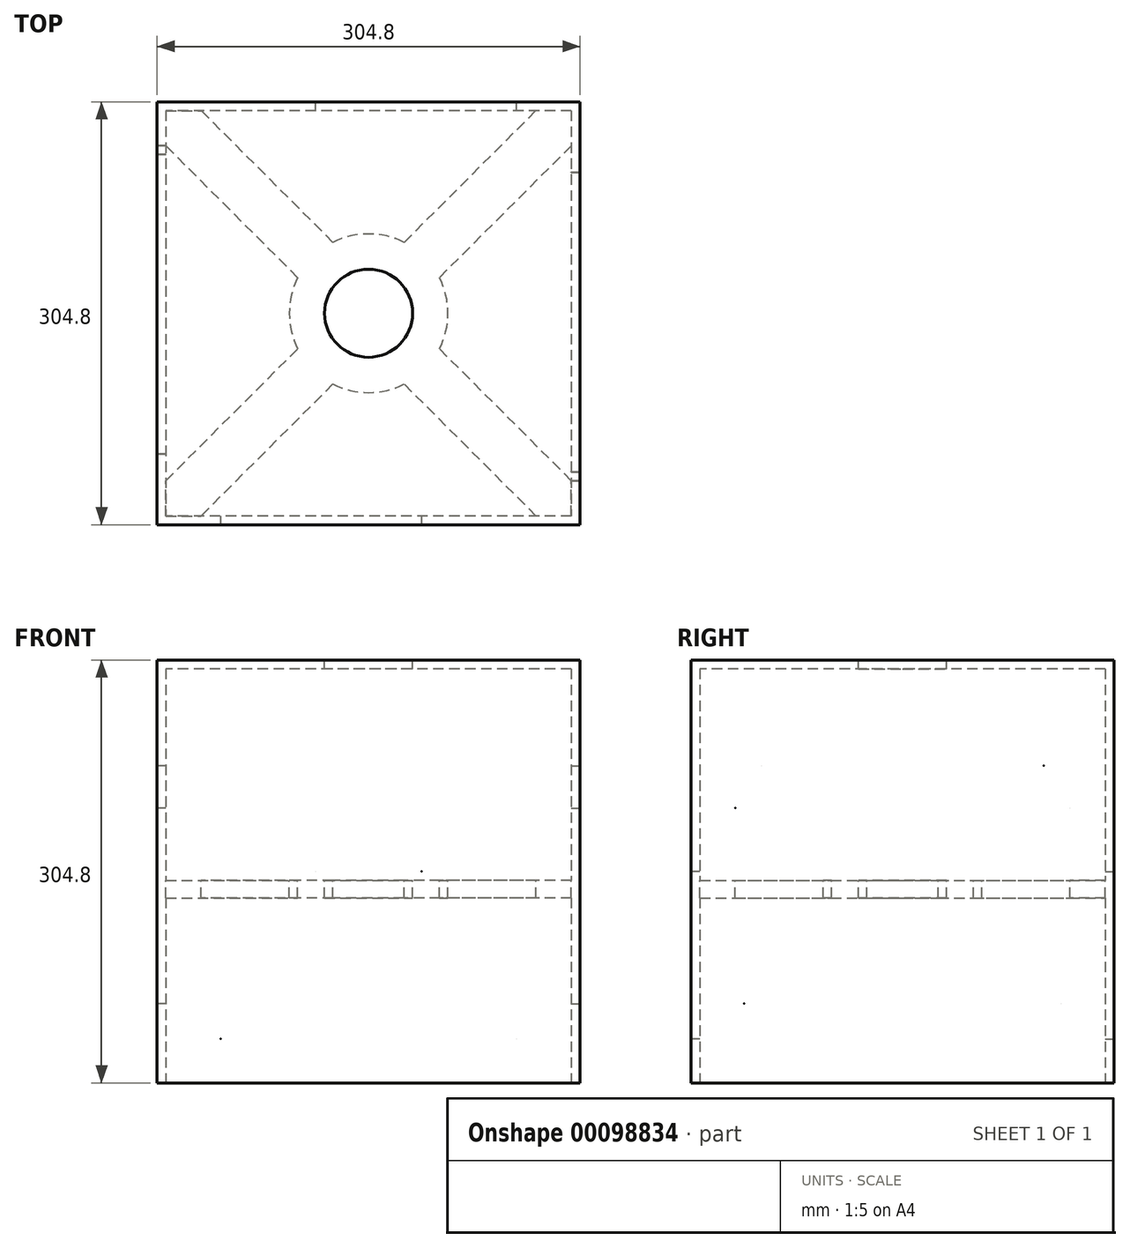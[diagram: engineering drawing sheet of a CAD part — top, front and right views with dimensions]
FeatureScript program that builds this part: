
annotation { "Feature Type Name" : "Feature", "Feature Type Description" : "" }
export const myFeature = defineFeature(function(context is Context, id is Id, definition is map)
    precondition{}
    {
        {
            var Q0;
            Q0=qCreatedBy(makeId("Top.planeOp"),FACE);
            var sketch = newSketch(context, id + "F0", { "sketchPlane" : qUnion([Q0])});
            skLineSegment(sketch, "E0.bottom", {"start": v(152.4, -152.4) * mm, "end": v(-152.4, -152.4) * mm});
            skLineSegment(sketch, "E0.top", {"start": v(152.4, 152.4) * mm, "end": v(-152.4, 152.4) * mm});
            skLineSegment(sketch, "E0.left", {"start": v(152.4, -152.4) * mm, "end": v(152.4, 152.4) * mm});
            skLineSegment(sketch, "E0.right", {"start": v(-152.4, -152.4) * mm, "end": v(-152.4, 152.4) * mm});
            skPoint(sketch, "E0.middle", {"position": v(0, 0) * mm});
            skLineSegment(sketch, "E1.bottom", {"start": v(146.05, 146.05) * mm, "end": v(-146.05, 146.05) * mm});
            skLineSegment(sketch, "E1.top", {"start": v(146.05, -146.05) * mm, "end": v(-146.05, -146.05) * mm});
            skLineSegment(sketch, "E1.left", {"start": v(146.05, 146.05) * mm, "end": v(146.05, -146.05) * mm});
            skLineSegment(sketch, "E1.right", {"start": v(-146.05, 146.05) * mm, "end": v(-146.05, -146.05) * mm});
            skSolve(sketch);
        }
        {
            var Q0;
            Q0 = qSketchRegion(id + "F0", true);
            extrude(context, id + "F1", {"entities" : qUnion([Q0]), "endBound" : BoundingType.SYMMETRIC, "depth" : 304.8 * mm});
        }
        {
            var Q0;
            Q0=makeQuery(id+"F1.opExtrude","CAP_FACE",FACE,{"disambiguationData":[OSD([sQuery(id+"F0.wireOp",EDGE,"E0.bottom"),sQuery(id+"F0.wireOp",EDGE,"E0.top"),sQuery(id+"F0.wireOp",EDGE,"E0.left"),sQuery(id+"F0.wireOp",EDGE,"E0.right"),sQuery(id+"F0.wireOp",EDGE,"E1.bottom"),sQuery(id+"F0.wireOp",EDGE,"E1.top"),sQuery(id+"F0.wireOp",EDGE,"E1.left"),sQuery(id+"F0.wireOp",EDGE,"E1.right")])],"isStart":false});
            var sketch = newSketch(context, id + "F2", { "sketchPlane" : qUnion([Q0])});
            skLineSegment(sketch, "E2.bottom", {"start": v(152.4, -152.4) * mm, "end": v(-152.4, -152.4) * mm});
            skLineSegment(sketch, "E2.top", {"start": v(152.4, 152.4) * mm, "end": v(-152.4, 152.4) * mm});
            skLineSegment(sketch, "E2.left", {"start": v(152.4, -152.4) * mm, "end": v(152.4, 152.4) * mm});
            skLineSegment(sketch, "E2.right", {"start": v(-152.4, -152.4) * mm, "end": v(-152.4, 152.4) * mm});
            skPoint(sketch, "E2.middle", {"position": v(0, 0) * mm});
            skSolve(sketch);
        }
        {
            var Q0;
            Q0 = qSketchRegion(id + "F2", true);
            extrude(context, id + "F3", {"entities" : qUnion([Q0]), "operationType" : NewBodyOperationType.ADD, "oppositeDirection" : true, "depth" : 6.35 * mm});
        }
        {
            var Q0;
            Q0=makeQuery(id+"F1.opExtrude","SWEPT_FACE",FACE,{"disambiguationData":[OSD([sQuery(id+"F0.wireOp",EDGE,"E0.bottom")])]});
            var sketch = newSketch(context, id + "F4", { "sketchPlane" : qUnion([Q0])});
            skLineSegment(sketch, "E3", {"start": v(-152.4, 152.4) * mm, "end": v(152.4, -152.4) * mm});
            skLineSegment(sketch, "E4", {"start": v(152.4, 152.4) * mm, "end": v(-152.4, -152.4) * mm});
            skLineSegment(sketch, "E5", {"start": v(152.4, 0) * mm, "end": v(-152.4, 0) * mm});
            skLineSegment(sketch, "E6", {"start": v(0, 152.4) * mm, "end": v(0, -152.4) * mm});
            skLineSegment(sketch, "E7", {"start": v(0, -152.4) * mm, "end": v(-152.4, 0) * mm});
            skLineSegment(sketch, "E8", {"start": v(-152.4, 0) * mm, "end": v(0, 152.4) * mm});
            skLineSegment(sketch, "E9", {"start": v(0, 152.4) * mm, "end": v(152.4, 0) * mm});
            skLineSegment(sketch, "E10", {"start": v(152.4, 0) * mm, "end": v(0, -152.4) * mm});
            skPoint(sketch, "E11", {"position": v(38.1, 0) * mm});
            skPoint(sketch, "E12", {"position": v(-106.68, -120.65) * mm});
            skLineSegment(sketch, "E13.bottom", {"start": v(-152.4, 152.4) * mm, "end": v(152.4, 152.4) * mm});
            skLineSegment(sketch, "E13.top", {"start": v(-152.4, -152.4) * mm, "end": v(152.4, -152.4) * mm});
            skLineSegment(sketch, "E13.left", {"start": v(-152.4, 152.4) * mm, "end": v(-152.4, -152.4) * mm});
            skLineSegment(sketch, "E13.right", {"start": v(152.4, 152.4) * mm, "end": v(152.4, -152.4) * mm});
            skSolve(sketch);
        }
        {
            var Q0;
            Q0=sQuery(id+"F4.wireOp",VERTEX,"E11");
            var Q1;
            Q1=makeQuery(id+"F1.opExtrude","SWEPT_BODY",BODY,{"disambiguationData":[OSD([sQuery(id+"F0.wireOp",EDGE,"E0.bottom"),sQuery(id+"F0.wireOp",EDGE,"E0.top"),sQuery(id+"F0.wireOp",EDGE,"E0.left"),sQuery(id+"F0.wireOp",EDGE,"E0.right"),sQuery(id+"F0.wireOp",EDGE,"E1.bottom"),sQuery(id+"F0.wireOp",EDGE,"E1.top"),sQuery(id+"F0.wireOp",EDGE,"E1.left"),sQuery(id+"F0.wireOp",EDGE,"E1.right")])]});
            hole(context, id + "F5", {"style" : HoleStyle.SIMPLE, "endStyle" : HoleEndStyle.BLIND, "holeDiameter" : 0.03 * mm, "holeDepth" : 12.7 * mm, "locations" : qUnion([Q0]), "scope" : qUnion([Q1])});
        }
        {
            var Q0;
            Q0=sQuery(id+"F4.wireOp",VERTEX,"E12");
            var Q1;
            Q1=makeQuery(id+"F1.opExtrude","SWEPT_BODY",BODY,{"disambiguationData":[OSD([sQuery(id+"F0.wireOp",EDGE,"E0.bottom"),sQuery(id+"F0.wireOp",EDGE,"E0.top"),sQuery(id+"F0.wireOp",EDGE,"E0.left"),sQuery(id+"F0.wireOp",EDGE,"E0.right"),sQuery(id+"F0.wireOp",EDGE,"E1.bottom"),sQuery(id+"F0.wireOp",EDGE,"E1.top"),sQuery(id+"F0.wireOp",EDGE,"E1.left"),sQuery(id+"F0.wireOp",EDGE,"E1.right")])]});
            hole(context, id + "F6", {"style" : HoleStyle.SIMPLE, "endStyle" : HoleEndStyle.BLIND, "holeDiameter" : 0.03 * mm, "holeDepth" : 12.7 * mm, "locations" : qUnion([Q0]), "scope" : qUnion([Q1])});
        }
        {
            var Q0;
            Q0=makeQuery(id+"F1.opExtrude","SWEPT_FACE",FACE,{"disambiguationData":[OSD([sQuery(id+"F0.wireOp",EDGE,"E0.top")])]});
            var sketch = newSketch(context, id + "F7", { "sketchPlane" : qUnion([Q0])});
            skLineSegment(sketch, "E14.bottom", {"start": v(-152.4, 152.4) * mm, "end": v(152.4, 152.4) * mm});
            skLineSegment(sketch, "E14.top", {"start": v(-152.4, -152.4) * mm, "end": v(152.4, -152.4) * mm});
            skLineSegment(sketch, "E14.left", {"start": v(-152.4, 152.4) * mm, "end": v(-152.4, -152.4) * mm});
            skLineSegment(sketch, "E14.right", {"start": v(152.4, 152.4) * mm, "end": v(152.4, -152.4) * mm});
            skLineSegment(sketch, "E15", {"start": v(-152.4, 152.4) * mm, "end": v(152.4, -152.4) * mm});
            skLineSegment(sketch, "E16", {"start": v(-152.4, -152.4) * mm, "end": v(152.4, 152.4) * mm});
            skLineSegment(sketch, "E17", {"start": v(0, 152.4) * mm, "end": v(0, -152.4) * mm});
            skLineSegment(sketch, "E18", {"start": v(0, -152.4) * mm, "end": v(-152.4, 0) * mm});
            skLineSegment(sketch, "E19", {"start": v(-152.4, 0) * mm, "end": v(0, 152.4) * mm});
            skLineSegment(sketch, "E20", {"start": v(0, 152.4) * mm, "end": v(152.4, 0) * mm});
            skLineSegment(sketch, "E21", {"start": v(152.4, 0) * mm, "end": v(0, -152.4) * mm});
            skLineSegment(sketch, "E22", {"start": v(-152.4, 0) * mm, "end": v(152.4, 0) * mm});
            skPoint(sketch, "E23", {"position": v(38.1, 0) * mm});
            skPoint(sketch, "E24", {"position": v(-106.68, -120.65) * mm});
            skSolve(sketch);
        }
        {
            var Q0;
            Q0=sQuery(id+"F7.wireOp",VERTEX,"E24");
            var Q1;
            Q1=makeQuery(id+"F1.opExtrude","SWEPT_BODY",BODY,{"disambiguationData":[OSD([sQuery(id+"F0.wireOp",EDGE,"E0.bottom"),sQuery(id+"F0.wireOp",EDGE,"E0.top"),sQuery(id+"F0.wireOp",EDGE,"E0.left"),sQuery(id+"F0.wireOp",EDGE,"E0.right"),sQuery(id+"F0.wireOp",EDGE,"E1.bottom"),sQuery(id+"F0.wireOp",EDGE,"E1.top"),sQuery(id+"F0.wireOp",EDGE,"E1.left"),sQuery(id+"F0.wireOp",EDGE,"E1.right")])]});
            hole(context, id + "F8", {"style" : HoleStyle.SIMPLE, "endStyle" : HoleEndStyle.BLIND, "holeDiameter" : 0.03 * mm, "holeDepth" : 12.7 * mm, "locations" : qUnion([Q0]), "scope" : qUnion([Q1])});
        }
        {
            var Q0;
            Q0=sQuery(id+"F7.wireOp",VERTEX,"E23");
            var Q1;
            Q1=makeQuery(id+"F1.opExtrude","SWEPT_BODY",BODY,{"disambiguationData":[OSD([sQuery(id+"F0.wireOp",EDGE,"E0.bottom"),sQuery(id+"F0.wireOp",EDGE,"E0.top"),sQuery(id+"F0.wireOp",EDGE,"E0.left"),sQuery(id+"F0.wireOp",EDGE,"E0.right"),sQuery(id+"F0.wireOp",EDGE,"E1.bottom"),sQuery(id+"F0.wireOp",EDGE,"E1.top"),sQuery(id+"F0.wireOp",EDGE,"E1.left"),sQuery(id+"F0.wireOp",EDGE,"E1.right")])]});
            hole(context, id + "F9", {"style" : HoleStyle.SIMPLE, "endStyle" : HoleEndStyle.BLIND, "holeDiameter" : 0.03 * mm, "holeDepth" : 12.7 * mm, "locations" : qUnion([Q0]), "scope" : qUnion([Q1])});
        }
        {
            var Q0;
            Q0=makeQuery(id+"F1.opExtrude","SWEPT_FACE",FACE,{"disambiguationData":[OSD([sQuery(id+"F0.wireOp",EDGE,"E0.left")])]});
            var sketch = newSketch(context, id + "F10", { "sketchPlane" : qUnion([Q0])});
            skLineSegment(sketch, "E25.bottom", {"start": v(-152.4, 152.4) * mm, "end": v(152.4, 152.4) * mm});
            skLineSegment(sketch, "E25.top", {"start": v(-152.4, -152.4) * mm, "end": v(152.4, -152.4) * mm});
            skLineSegment(sketch, "E25.left", {"start": v(-152.4, 152.4) * mm, "end": v(-152.4, -152.4) * mm});
            skLineSegment(sketch, "E25.right", {"start": v(152.4, 152.4) * mm, "end": v(152.4, -152.4) * mm});
            skLineSegment(sketch, "E26", {"start": v(-152.4, 152.4) * mm, "end": v(152.4, -152.4) * mm});
            skLineSegment(sketch, "E27", {"start": v(-152.4, -152.4) * mm, "end": v(152.4, 152.4) * mm});
            skLineSegment(sketch, "E28", {"start": v(-152.4, 0) * mm, "end": v(152.4, 0) * mm});
            skLineSegment(sketch, "E29", {"start": v(0, 152.4) * mm, "end": v(0, -152.4) * mm});
            skLineSegment(sketch, "E30", {"start": v(0, -152.4) * mm, "end": v(-152.4, 0) * mm});
            skLineSegment(sketch, "E31", {"start": v(-152.4, 0) * mm, "end": v(0, 152.4) * mm});
            skLineSegment(sketch, "E32", {"start": v(0, 152.4) * mm, "end": v(152.4, 0) * mm});
            skLineSegment(sketch, "E33", {"start": v(152.4, 0) * mm, "end": v(0, -152.4) * mm});
            skPoint(sketch, "E34", {"position": v(-114.3, -95.25) * mm});
            skPoint(sketch, "E35", {"position": v(-120.65, 45.72) * mm});
            skPoint(sketch, "E36", {"position": v(101.6, 76.2) * mm});
            skSolve(sketch);
        }
        {
            var Q0;
            Q0=makeQuery(id+"F1.opExtrude","SWEPT_FACE",FACE,{"disambiguationData":[OSD([sQuery(id+"F0.wireOp",EDGE,"E0.right")])]});
            var sketch = newSketch(context, id + "F11", { "sketchPlane" : qUnion([Q0])});
            skLineSegment(sketch, "E37.bottom", {"start": v(-152.4, 152.4) * mm, "end": v(152.4, 152.4) * mm});
            skLineSegment(sketch, "E37.top", {"start": v(-152.4, -152.4) * mm, "end": v(152.4, -152.4) * mm});
            skLineSegment(sketch, "E37.left", {"start": v(-152.4, 152.4) * mm, "end": v(-152.4, -152.4) * mm});
            skLineSegment(sketch, "E37.right", {"start": v(152.4, 152.4) * mm, "end": v(152.4, -152.4) * mm});
            skLineSegment(sketch, "E38", {"start": v(-152.4, 152.4) * mm, "end": v(152.4, -152.4) * mm});
            skLineSegment(sketch, "E39", {"start": v(0, -152.4) * mm, "end": v(0, 152.4) * mm});
            skLineSegment(sketch, "E40", {"start": v(0, 152.4) * mm, "end": v(-152.4, 0) * mm});
            skLineSegment(sketch, "E41", {"start": v(-152.4, 0) * mm, "end": v(152.4, 0) * mm});
            skLineSegment(sketch, "E42", {"start": v(152.4, 0) * mm, "end": v(0, 152.4) * mm});
            skLineSegment(sketch, "E43", {"start": v(0, -152.4) * mm, "end": v(-152.4, 0) * mm});
            skLineSegment(sketch, "E44", {"start": v(-152.4, -152.4) * mm, "end": v(152.4, 152.4) * mm});
            skLineSegment(sketch, "E45", {"start": v(152.4, 0) * mm, "end": v(0, -152.4) * mm});
            skPoint(sketch, "E46", {"position": v(-120.65, 45.72) * mm});
            skPoint(sketch, "E47", {"position": v(-114.3, -95.25) * mm});
            skPoint(sketch, "E48", {"position": v(101.6, 76.2) * mm});
            skSolve(sketch);
        }
        {
            var Q0;
            Q0=sQuery(id+"F10.wireOp",VERTEX,"E34");
            var Q1;
            Q1=makeQuery(id+"F1.opExtrude","SWEPT_BODY",BODY,{"disambiguationData":[OSD([sQuery(id+"F0.wireOp",EDGE,"E0.bottom"),sQuery(id+"F0.wireOp",EDGE,"E0.top"),sQuery(id+"F0.wireOp",EDGE,"E0.left"),sQuery(id+"F0.wireOp",EDGE,"E0.right"),sQuery(id+"F0.wireOp",EDGE,"E1.bottom"),sQuery(id+"F0.wireOp",EDGE,"E1.top"),sQuery(id+"F0.wireOp",EDGE,"E1.left"),sQuery(id+"F0.wireOp",EDGE,"E1.right")])]});
            hole(context, id + "F12", {"style" : HoleStyle.SIMPLE, "endStyle" : HoleEndStyle.BLIND, "holeDiameter" : 0.03 * mm, "holeDepth" : 12.7 * mm, "locations" : qUnion([Q0]), "scope" : qUnion([Q1])});
        }
        {
            var Q0;
            Q0=sQuery(id+"F10.wireOp",VERTEX,"E35");
            var Q1;
            Q1=makeQuery(id+"F1.opExtrude","SWEPT_BODY",BODY,{"disambiguationData":[OSD([sQuery(id+"F0.wireOp",EDGE,"E0.bottom"),sQuery(id+"F0.wireOp",EDGE,"E0.top"),sQuery(id+"F0.wireOp",EDGE,"E0.left"),sQuery(id+"F0.wireOp",EDGE,"E0.right"),sQuery(id+"F0.wireOp",EDGE,"E1.bottom"),sQuery(id+"F0.wireOp",EDGE,"E1.top"),sQuery(id+"F0.wireOp",EDGE,"E1.left"),sQuery(id+"F0.wireOp",EDGE,"E1.right")])]});
            hole(context, id + "F13", {"style" : HoleStyle.SIMPLE, "endStyle" : HoleEndStyle.BLIND, "holeDiameter" : 0.03 * mm, "holeDepth" : 12.7 * mm, "locations" : qUnion([Q0]), "scope" : qUnion([Q1])});
        }
        {
            var Q0;
            Q0=sQuery(id+"F11.wireOp",VERTEX,"E47");
            var Q1;
            Q1=makeQuery(id+"F1.opExtrude","SWEPT_BODY",BODY,{"disambiguationData":[OSD([sQuery(id+"F0.wireOp",EDGE,"E0.bottom"),sQuery(id+"F0.wireOp",EDGE,"E0.top"),sQuery(id+"F0.wireOp",EDGE,"E0.left"),sQuery(id+"F0.wireOp",EDGE,"E0.right"),sQuery(id+"F0.wireOp",EDGE,"E1.bottom"),sQuery(id+"F0.wireOp",EDGE,"E1.top"),sQuery(id+"F0.wireOp",EDGE,"E1.left"),sQuery(id+"F0.wireOp",EDGE,"E1.right")])]});
            hole(context, id + "F14", {"style" : HoleStyle.SIMPLE, "endStyle" : HoleEndStyle.BLIND, "holeDiameter" : 0.03 * mm, "holeDepth" : 12.7 * mm, "locations" : qUnion([Q0]), "scope" : qUnion([Q1])});
        }
        {
            var Q0;
            Q0=sQuery(id+"F11.wireOp",VERTEX,"E46");
            var Q1;
            Q1=makeQuery(id+"F1.opExtrude","SWEPT_BODY",BODY,{"disambiguationData":[OSD([sQuery(id+"F0.wireOp",EDGE,"E0.bottom"),sQuery(id+"F0.wireOp",EDGE,"E0.top"),sQuery(id+"F0.wireOp",EDGE,"E0.left"),sQuery(id+"F0.wireOp",EDGE,"E0.right"),sQuery(id+"F0.wireOp",EDGE,"E1.bottom"),sQuery(id+"F0.wireOp",EDGE,"E1.top"),sQuery(id+"F0.wireOp",EDGE,"E1.left"),sQuery(id+"F0.wireOp",EDGE,"E1.right")])]});
            hole(context, id + "F15", {"style" : HoleStyle.SIMPLE, "endStyle" : HoleEndStyle.BLIND, "holeDiameter" : 0.03 * mm, "holeDepth" : 12.7 * mm, "locations" : qUnion([Q0]), "scope" : qUnion([Q1])});
        }
        {
            var Q0;
            Q0=sQuery(id+"F11.wireOp",VERTEX,"E48");
            var Q1;
            Q1=makeQuery(id+"F1.opExtrude","SWEPT_BODY",BODY,{"disambiguationData":[OSD([sQuery(id+"F0.wireOp",EDGE,"E0.bottom"),sQuery(id+"F0.wireOp",EDGE,"E0.top"),sQuery(id+"F0.wireOp",EDGE,"E0.left"),sQuery(id+"F0.wireOp",EDGE,"E0.right"),sQuery(id+"F0.wireOp",EDGE,"E1.bottom"),sQuery(id+"F0.wireOp",EDGE,"E1.top"),sQuery(id+"F0.wireOp",EDGE,"E1.left"),sQuery(id+"F0.wireOp",EDGE,"E1.right")])]});
            hole(context, id + "F16", {"style" : HoleStyle.SIMPLE, "endStyle" : HoleEndStyle.BLIND, "holeDiameter" : 0.03 * mm, "holeDepth" : 12.7 * mm, "locations" : qUnion([Q0]), "scope" : qUnion([Q1])});
        }
        {
            var Q0;
            Q0=sQuery(id+"F10.wireOp",VERTEX,"E36");
            var Q1;
            Q1=makeQuery(id+"F1.opExtrude","SWEPT_BODY",BODY,{"disambiguationData":[OSD([sQuery(id+"F0.wireOp",EDGE,"E0.bottom"),sQuery(id+"F0.wireOp",EDGE,"E0.top"),sQuery(id+"F0.wireOp",EDGE,"E0.left"),sQuery(id+"F0.wireOp",EDGE,"E0.right"),sQuery(id+"F0.wireOp",EDGE,"E1.bottom"),sQuery(id+"F0.wireOp",EDGE,"E1.top"),sQuery(id+"F0.wireOp",EDGE,"E1.left"),sQuery(id+"F0.wireOp",EDGE,"E1.right")])]});
            hole(context, id + "F17", {"style" : HoleStyle.SIMPLE, "endStyle" : HoleEndStyle.BLIND, "holeDiameter" : 0.03 * mm, "holeDepth" : 12.7 * mm, "locations" : qUnion([Q0]), "scope" : qUnion([Q1])});
        }
        {
            var Q0;
            Q0=makeQuery(id+"F3.opExtrude","CAP_FACE",FACE,{"disambiguationData":[OSD([sQuery(id+"F2.wireOp",EDGE,"E2.bottom"),sQuery(id+"F2.wireOp",EDGE,"E2.top"),sQuery(id+"F2.wireOp",EDGE,"E2.left"),sQuery(id+"F2.wireOp",EDGE,"E2.right")])],"isStart":false});
            cPlane(context, id + "F18", {"entities" : qUnion([Q0]), "cplaneType" : CPlaneType.OFFSET, "offset" : 152.4 * mm, "width" : 152.4 * mm, "height" : 152.4 * mm});
        }
        {
            var Q0;
            Q0=qCreatedBy(id+"F18.planeOp",FACE);
            var sketch = newSketch(context, id + "F19", { "sketchPlane" : qUnion([Q0])});
            skCircle(sketch, "E49", {"center": v(0, 0) * mm, "radius": 31.75 * mm});
            skLineSegment(sketch, "E50.bottom", {"start": v(146.05, -146.05) * mm, "end": v(120.65, -146.05) * mm});
            skLineSegment(sketch, "E50.top", {"start": v(146.05, 146.05) * mm, "end": v(120.65, 146.05) * mm});
            skLineSegment(sketch, "E50.left", {"start": v(146.05, -146.05) * mm, "end": v(146.05, -120.65) * mm});
            skLineSegment(sketch, "E50.right", {"start": v(-146.05, -146.05) * mm, "end": v(-146.05, -120.65) * mm});
            skLineSegment(sketch, "E51.bottom", {"start": v(-146.05, 146.05) * mm, "end": v(-120.65, 146.05) * mm});
            skLineSegment(sketch, "E51.left", {"start": v(-146.05, 146.05) * mm, "end": v(-146.05, 120.65) * mm});
            skLineSegment(sketch, "E52.left", {"start": v(146.05, 146.05) * mm, "end": v(146.05, 120.65) * mm});
            skLineSegment(sketch, "E53.bottom", {"start": v(-146.05, -146.05) * mm, "end": v(-120.65, -146.05) * mm});
            skLineSegment(sketch, "E54", {"start": v(-146.05, 120.65) * mm, "end": v(-51.06, 25.66) * mm});
            skLineSegment(sketch, "E55", {"start": v(146.05, -120.65) * mm, "end": v(51.06, -25.66) * mm});
            skLineSegment(sketch, "E56", {"start": v(120.65, 146.05) * mm, "end": v(25.66, 51.06) * mm});
            skLineSegment(sketch, "E57", {"start": v(146.05, 120.65) * mm, "end": v(51.06, 25.66) * mm});
            skArc(sketch, "E58.0", {"start": v(-51.06, 25.66) * mm, "mid": v(-57.15, 0) * mm, "end": v(-51.06, -25.66) * mm});
            skLineSegment(sketch, "E59.trimOffspring", {"start": v(-25.66, 51.06) * mm, "end": v(-120.65, 146.05) * mm});
            skArc(sketch, "E60.trimOffspring", {"start": v(25.66, 51.06) * mm, "mid": v(0, 57.15) * mm, "end": v(-25.66, 51.06) * mm});
            skLineSegment(sketch, "E61.trimOffspring", {"start": v(-51.06, -25.66) * mm, "end": v(-146.05, -120.65) * mm});
            skLineSegment(sketch, "E62.trimOffspring", {"start": v(25.66, -51.06) * mm, "end": v(120.65, -146.05) * mm});
            skLineSegment(sketch, "E63.trimOffspring", {"start": v(-25.66, -51.06) * mm, "end": v(-120.65, -146.05) * mm});
            skArc(sketch, "E64.trimOffspring", {"start": v(51.06, -25.66) * mm, "mid": v(57.15, 0) * mm, "end": v(51.06, 25.66) * mm});
            skArc(sketch, "E65.trimOffspring", {"start": v(-25.66, -51.06) * mm, "mid": v(0, -57.15) * mm, "end": v(25.66, -51.06) * mm});
            skLineSegment(sketch, "E66.trimOffspring", {"start": v(-120.65, 146.05) * mm, "end": v(-146.05, 146.05) * mm});
            skLineSegment(sketch, "E67.trimOffspring", {"start": v(-146.05, 120.65) * mm, "end": v(-146.05, 146.05) * mm});
            skLineSegment(sketch, "E68.trimOffspring", {"start": v(-120.65, -146.05) * mm, "end": v(-146.05, -146.05) * mm});
            skLineSegment(sketch, "E69.trimOffspring", {"start": v(146.05, 120.65) * mm, "end": v(146.05, 146.05) * mm});
            skSolve(sketch);
        }
        {
            var Q0;
            Q0=makeQuery(id+"F19.imprint","IMPRINT",FACE,{"disambiguationData":[TD([[makeQuery(id+"F19.imprint","IMPRINT",EDGE,{"derivedFrom":sQuery(id+"F19.wireOp",EDGE,"E49")}),-1.0]])]});
            extrude(context, id + "F20", {"entities" : qUnion([Q0]), "operationType" : NewBodyOperationType.ADD, "depth" : 12.7 * mm});
        }
        {
            var Q0;
            Q0=makeQuery(id+"F3.boolean.opBoolean","MERGE",FACE,{"derivedFrom":[makeQuery(id+"F1.opExtrude","CAP_FACE",FACE,{"disambiguationData":[OSD([sQuery(id+"F0.wireOp",EDGE,"E0.bottom"),sQuery(id+"F0.wireOp",EDGE,"E0.top"),sQuery(id+"F0.wireOp",EDGE,"E0.left"),sQuery(id+"F0.wireOp",EDGE,"E0.right"),sQuery(id+"F0.wireOp",EDGE,"E1.bottom"),sQuery(id+"F0.wireOp",EDGE,"E1.top"),sQuery(id+"F0.wireOp",EDGE,"E1.left"),sQuery(id+"F0.wireOp",EDGE,"E1.right")])],"isStart":false}),makeQuery(id+"F3.opExtrude","CAP_FACE",FACE,{"disambiguationData":[OSD([sQuery(id+"F2.wireOp",EDGE,"E2.bottom"),sQuery(id+"F2.wireOp",EDGE,"E2.top"),sQuery(id+"F2.wireOp",EDGE,"E2.left"),sQuery(id+"F2.wireOp",EDGE,"E2.right")])],"isStart":true})]});
            var sketch = newSketch(context, id + "F21", { "sketchPlane" : qUnion([Q0])});
            skCircle(sketch, "E70", {"center": v(0, 0) * mm, "radius": 31.75 * mm});
            skSolve(sketch);
        }
        {
            var Q0;
            Q0 = qSketchRegion(id + "F21", true);
            extrude(context, id + "F22", {"entities" : qUnion([Q0]), "operationType" : NewBodyOperationType.REMOVE, "oppositeDirection" : true, "depth" : 25.4 * mm});
        }
    });
